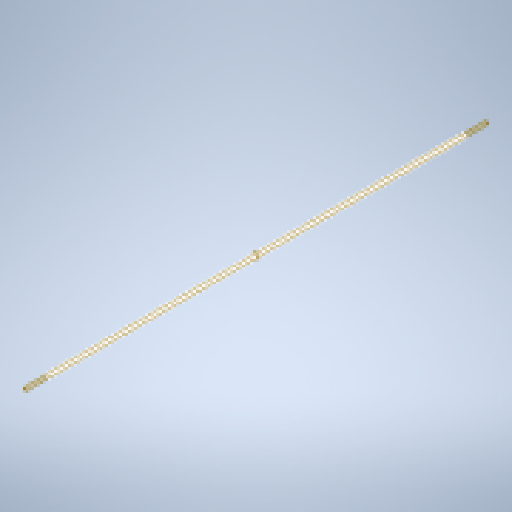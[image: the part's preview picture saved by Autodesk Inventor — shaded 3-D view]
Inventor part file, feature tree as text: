
AUTODESK INVENTOR PART (.ipt)
format: ipt  version: 2025.2 (Build 292293000, 293)  size: 358,400 bytes
history: native  units: mm
features: mirror x2, other x1, extrude x1, sketch x1
ambient origin geometry x8: Origin, YZ Plane, XZ Plane, XY Plane, X Axis, Y Axis, Z Axis, Center Point
bodies: Body1 (feature_tree)
feature tree (5):
  other  "Sólido1"
  extrude  "Extrusão1"  Depth=5.0mm
  mirror  "Espelhar1"
  mirror  "Espelhar2"
  sketch  "Esboço1"  dims[d0=20.0mm d2=5.0mm d3=6.0mm d5=2.0mm d7=1.0mm d8=6.0mm d9=1.0mm d10=0.5mm d11=0.5mm d12=0.5mm d14=0.5mm d15=0.5mm d16=10.0mm d17=2.5mm d18=1000.0mm d19=0.0mm d20=0.5mm d21=0.5mm]
